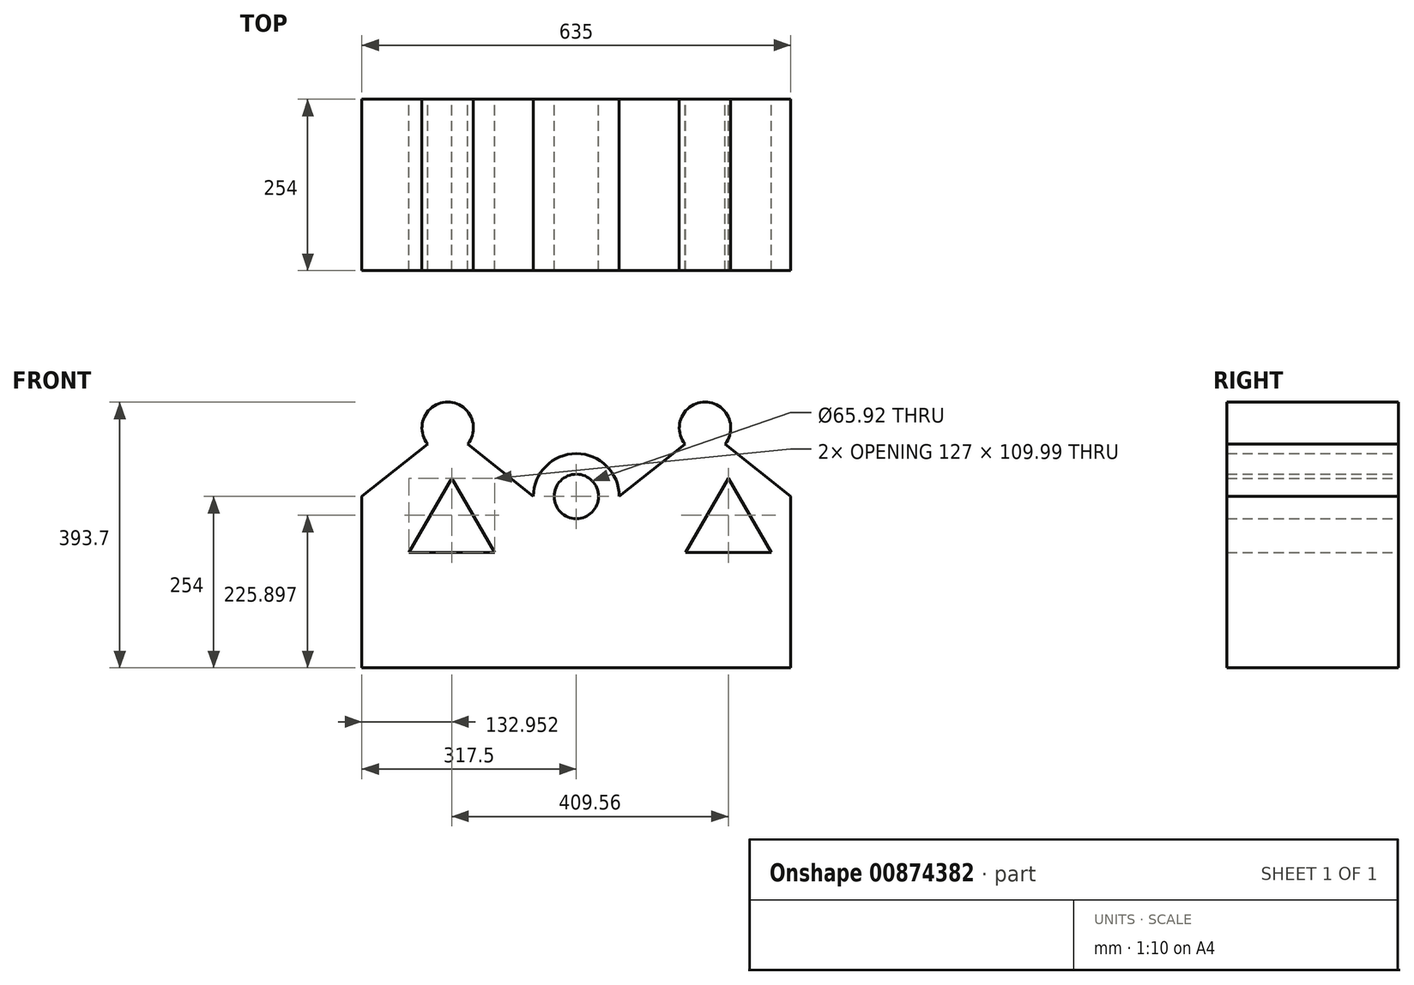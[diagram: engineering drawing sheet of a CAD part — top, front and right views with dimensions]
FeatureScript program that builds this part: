
annotation { "Feature Type Name" : "Feature", "Feature Type Description" : "" }
export const myFeature = defineFeature(function(context is Context, id is Id, definition is map)
    precondition{}
    {
        {
            var Q0;
            Q0=qCreatedBy(makeId("Front.planeOp"),FACE);
            var sketch = newSketch(context, id + "F0", { "sketchPlane" : qUnion([Q0])});
            skLineSegment(sketch, "E0", {"start": v(0, 0) * mm, "end": v(127, 0) * mm});
            skLineSegment(sketch, "E1", {"start": v(127, 0) * mm, "end": v(127, 254) * mm});
            skLineSegment(sketch, "E2", {"start": v(0, 0) * mm, "end": v(0, 254) * mm});
            skArc(sketch, "E3", {"start": v(127, 254) * mm, "mid": v(63.5, 317.5) * mm, "end": v(0, 254) * mm});
            skCircle(sketch, "E4", {"center": v(63.5, 254) * mm, "radius": 32.96 * mm});
            skLineSegment(sketch, "E5", {"start": v(0, 0) * mm, "end": v(-254, 0) * mm});
            skLineSegment(sketch, "E6", {"start": v(-254, 0) * mm, "end": v(-254, 254) * mm});
            skLineSegment(sketch, "E7", {"start": v(-156.75, 331.8) * mm, "end": v(-254, 254) * mm});
            skLineSegment(sketch, "E8", {"start": v(-97.25, 331.8) * mm, "end": v(0, 254) * mm});
            skLineSegment(sketch, "E9", {"start": v(127, 0) * mm, "end": v(381, 0) * mm});
            skLineSegment(sketch, "E10", {"start": v(381, 254) * mm, "end": v(381, 0) * mm});
            skLineSegment(sketch, "E11", {"start": v(224.25, 331.8) * mm, "end": v(127, 254) * mm});
            skLineSegment(sketch, "E12", {"start": v(283.75, 331.8) * mm, "end": v(381, 254) * mm});
            skArc(sketch, "E13", {"start": v(-97.25, 331.8) * mm, "mid": v(-127, 393.7) * mm, "end": v(-156.75, 331.8) * mm});
            skArc(sketch, "E14", {"start": v(283.75, 331.8) * mm, "mid": v(254, 393.7) * mm, "end": v(224.25, 331.8) * mm});
            skSolve(sketch);
        }
        {
            var Q0;
            Q0=makeQuery(id+"F0.imprint","IMPRINT",FACE,{"disambiguationData":[TD([[makeQuery(id+"F0.imprint","IMPRINT",EDGE,{"derivedFrom":sQuery(id+"F0.wireOp",EDGE,"E2")}),1.0]])]});
            var Q1;
            Q1=makeQuery(id+"F0.imprint","IMPRINT",FACE,{"disambiguationData":[TD([[makeQuery(id+"F0.imprint","IMPRINT",EDGE,{"derivedFrom":sQuery(id+"F0.wireOp",EDGE,"E1")}),-1.0]])]});
            var Q2;
            Q2=makeQuery(id+"F0.imprint","IMPRINT",FACE,{"disambiguationData":[TD([[makeQuery(id+"F0.imprint","IMPRINT",EDGE,{"derivedFrom":sQuery(id+"F0.wireOp",EDGE,"E0")}),1.0]])]});
            extrude(context, id + "F1", {"entities" : qUnion([Q0, Q1, Q2]), "depth" : 254 * mm, "offsetDistance" : 25.4 * mm});
        }
        {
            var Q0;
            Q0=qCreatedBy(makeId("Front.planeOp"),FACE);
            var sketch = newSketch(context, id + "F2", { "sketchPlane" : qUnion([Q0])});
            skLineSegment(sketch, "E15", {"start": v(-121.05, 280.9) * mm, "end": v(-184.55, 170.9) * mm});
            skLineSegment(sketch, "E16", {"start": v(-184.55, 170.9) * mm, "end": v(-57.55, 170.9) * mm});
            skLineSegment(sketch, "E17", {"start": v(-57.55, 170.9) * mm, "end": v(-121.05, 280.9) * mm});
            skLineSegment(sketch, "E18", {"start": v(225.01, 170.9) * mm, "end": v(352.01, 170.9) * mm});
            skLineSegment(sketch, "E19", {"start": v(352.01, 170.9) * mm, "end": v(288.51, 280.9) * mm});
            skLineSegment(sketch, "E20", {"start": v(288.51, 280.9) * mm, "end": v(225.01, 170.9) * mm});
            skSolve(sketch);
        }
        {
            var Q0;
            Q0=makeQuery(id+"F2.imprint","IMPRINT",FACE,{"disambiguationData":[TD([[makeQuery(id+"F2.imprint","IMPRINT",EDGE,{"derivedFrom":sQuery(id+"F2.wireOp",EDGE,"E18")}),1.0]])]});
            var Q1;
            Q1=makeQuery(id+"F2.imprint","IMPRINT",FACE,{"disambiguationData":[TD([[makeQuery(id+"F2.imprint","IMPRINT",EDGE,{"derivedFrom":sQuery(id+"F2.wireOp",EDGE,"E15")}),1.0]])]});
            extrude(context, id + "F3", {"entities" : qUnion([Q0, Q1]), "operationType" : NewBodyOperationType.REMOVE, "endBound" : BoundingType.THROUGH_ALL, "depth" : 25.4 * mm, "offsetDistance" : 25.4 * mm});
        }
    });
